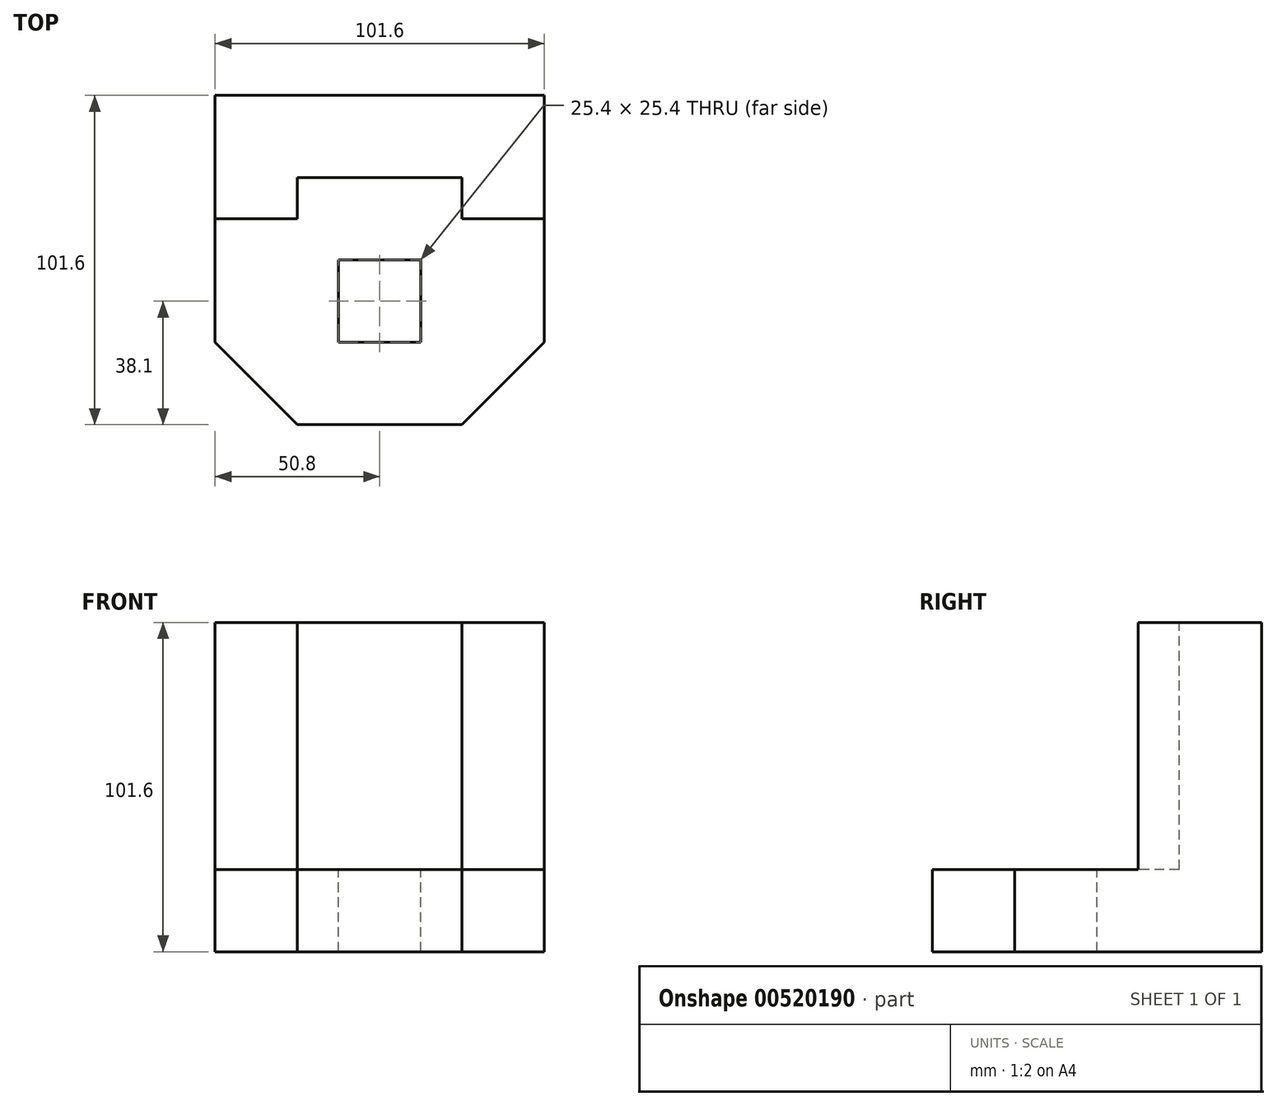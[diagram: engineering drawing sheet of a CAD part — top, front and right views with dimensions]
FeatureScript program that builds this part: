
annotation { "Feature Type Name" : "Feature", "Feature Type Description" : "" }
export const myFeature = defineFeature(function(context is Context, id is Id, definition is map)
    precondition{}
    {
        {
            var Q0;
            Q0=qCreatedBy(makeId("Right.planeOp"),FACE);
            var sketch = newSketch(context, id + "F0", { "sketchPlane" : qUnion([Q0])});
            skLineSegment(sketch, "E0.bottom", {"start": v(0, 0) * mm, "end": v(101.6, 0) * mm});
            skLineSegment(sketch, "E0.top", {"start": v(0, -101.6) * mm, "end": v(101.6, -101.6) * mm});
            skLineSegment(sketch, "E0.left", {"start": v(0, 0) * mm, "end": v(0, -101.6) * mm});
            skLineSegment(sketch, "E0.right", {"start": v(101.6, 0) * mm, "end": v(101.6, -101.6) * mm});
            skSolve(sketch);
        }
        {
            var Q0;
            Q0=makeQuery(id+"F0.imprint","IMPRINT",FACE,{"disambiguationData":[TD([[makeQuery(id+"F0.imprint","IMPRINT",EDGE,{"derivedFrom":sQuery(id+"F0.wireOp",EDGE,"E0.bottom")}),-1.0]])]});
            extrude(context, id + "F1", {"entities" : qUnion([Q0]), "oppositeDirection" : true, "depth" : 101.6 * mm, "offsetDistance" : 25.4 * mm});
        }
        {
            var Q0;
            Q0=makeQuery(id+"F1.opExtrude","SWEPT_FACE",FACE,{"disambiguationData":[OSD([sQuery(id+"F0.wireOp",EDGE,"E0.bottom")])]});
            var sketch = newSketch(context, id + "F2", { "sketchPlane" : qUnion([Q0])});
            skLineSegment(sketch, "E1", {"start": v(-101.6, 101.6) * mm, "end": v(-101.6, 63.5) * mm});
            skLineSegment(sketch, "E2", {"start": v(-101.6, 63.5) * mm, "end": v(-76.2, 63.5) * mm});
            skLineSegment(sketch, "E3", {"start": v(-76.2, 63.5) * mm, "end": v(-76.2, 82.55) * mm});
            skPoint(sketch, "E3.endSnap0", {"position": v(-101.6, 82.55) * mm});
            skLineSegment(sketch, "E4", {"start": v(-76.2, 82.55) * mm, "end": v(-25.4, 82.55) * mm});
            skLineSegment(sketch, "E5", {"start": v(-25.4, 82.55) * mm, "end": v(-25.4, 63.5) * mm});
            skLineSegment(sketch, "E6", {"start": v(-25.4, 63.5) * mm, "end": v(0, 63.5) * mm});
            skLineSegment(sketch, "E7", {"start": v(0, 63.5) * mm, "end": v(-76.2, 63.5) * mm});
            skLineSegment(sketch, "E8", {"start": v(-25.4, 63.5) * mm, "end": v(-76.2, 63.5) * mm});
            skSolve(sketch);
        }
        {
            var Q0;
            {var subQ3=sQuery(id+"F2.wireOp",EDGE,"E2");Q0=makeQuery(id+"F2.imprint","IMPRINT",FACE,{"disambiguationData":[TD([[makeQuery(id+"F2.imprint","IMPRINT",EDGE,{"derivedFrom":subQ3}),-1.0]])]});}
            extrude(context, id + "F3", {"entities" : qUnion([Q0]), "operationType" : NewBodyOperationType.REMOVE, "oppositeDirection" : true, "depth" : 76.2 * mm, "offsetDistance" : 25.4 * mm});
        }
        {
            var Q0;
            Q0=makeQuery(id+"F1.opExtrude","SWEPT_FACE",FACE,{"disambiguationData":[OSD([sQuery(id+"F0.wireOp",EDGE,"E0.bottom")])]});
            var sketch = newSketch(context, id + "F4", { "sketchPlane" : qUnion([Q0])});
            skLineSegment(sketch, "E9", {"start": v(-101.6, 101.6) * mm, "end": v(-101.6, 63.5) * mm});
            skLineSegment(sketch, "E10", {"start": v(-101.6, 63.5) * mm, "end": v(-76.2, 63.5) * mm});
            skLineSegment(sketch, "E11", {"start": v(-76.2, 63.5) * mm, "end": v(-76.2, 76.2) * mm});
            skLineSegment(sketch, "E12", {"start": v(-76.2, 76.2) * mm, "end": v(-25.4, 76.2) * mm});
            skLineSegment(sketch, "E13", {"start": v(-25.4, 76.2) * mm, "end": v(-25.4, 63.5) * mm});
            skLineSegment(sketch, "E14", {"start": v(-25.4, 63.5) * mm, "end": v(0, 63.5) * mm});
            skLineSegment(sketch, "E15", {"start": v(0, 63.5) * mm, "end": v(-25.4, 63.5) * mm});
            skLineSegment(sketch, "E16", {"start": v(-76.2, 63.5) * mm, "end": v(-25.4, 63.5) * mm});
            skSolve(sketch);
        }
        {
            var Q0;
            Q0=makeQuery(id+"F4.imprint","IMPRINT",FACE,{"disambiguationData":[TD([[makeQuery(id+"F4.imprint","IMPRINT",EDGE,{"derivedFrom":sQuery(id+"F4.wireOp",EDGE,"E11")}),-1.0]])]});
            extrude(context, id + "F5", {"entities" : qUnion([Q0]), "operationType" : NewBodyOperationType.REMOVE, "oppositeDirection" : true, "depth" : 76.2 * mm, "offsetDistance" : 25.4 * mm});
        }
        {
            var Q0;
            Q0=makeQuery(id+"F3.boolean.opBoolean","COPY",FACE,{"derivedFrom":makeQuery(id+"F3.opExtrude","CAP_FACE",FACE,{"disambiguationData":[OSD([sQuery(id+"F0.wireOp",EDGE,"E0.bottom"),sQuery(id+"F0.wireOp",EDGE,"E0.left"),sQuery(id+"F2.wireOp",EDGE,"E2"),sQuery(id+"F2.wireOp",EDGE,"E7"),sQuery(id+"F2.wireOp",EDGE,"E8")])],"isStart":false})});
            var sketch = newSketch(context, id + "F6", { "sketchPlane" : qUnion([Q0])});
            skLineSegment(sketch, "E17.bottom", {"start": v(-101.6, 0) * mm, "end": v(-76.2, 0) * mm});
            skLineSegment(sketch, "E17.top", {"start": v(-101.6, 25.4) * mm, "end": v(-76.2, 25.4) * mm});
            skLineSegment(sketch, "E17.left", {"start": v(-101.6, 0) * mm, "end": v(-101.6, 25.4) * mm});
            skLineSegment(sketch, "E17.right", {"start": v(-76.2, 0) * mm, "end": v(-76.2, 25.4) * mm});
            skLineSegment(sketch, "E18.bottom", {"start": v(0, 0) * mm, "end": v(-25.4, 0) * mm});
            skLineSegment(sketch, "E18.top", {"start": v(0, 25.4) * mm, "end": v(-25.4, 25.4) * mm});
            skLineSegment(sketch, "E18.left", {"start": v(0, 0) * mm, "end": v(0, 25.4) * mm});
            skLineSegment(sketch, "E18.right", {"start": v(-25.4, 0) * mm, "end": v(-25.4, 25.4) * mm});
            skLineSegment(sketch, "E19", {"start": v(-76.2, 76.2) * mm, "end": v(-76.2, 50.8) * mm});
            skLineSegment(sketch, "E20", {"start": v(-76.2, 50.8) * mm, "end": v(-76.2, 76.2) * mm});
            skLineSegment(sketch, "E21", {"start": v(-25.4, 76.2) * mm, "end": v(-76.2, 76.2) * mm});
            skLineSegment(sketch, "E22", {"start": v(-25.4, 76.2) * mm, "end": v(-25.4, 50.8) * mm});
            skLineSegment(sketch, "E23", {"start": v(-25.4, 50.8) * mm, "end": v(-76.2, 50.8) * mm});
            skLineSegment(sketch, "E24", {"start": v(-76.2, 25.4) * mm, "end": v(-76.2, 50.8) * mm});
            skLineSegment(sketch, "E25", {"start": v(-25.4, 50.8) * mm, "end": v(-25.4, 25.4) * mm});
            skLineSegment(sketch, "E26", {"start": v(-76.2, 25.4) * mm, "end": v(-25.4, 25.4) * mm});
            skLineSegment(sketch, "E27", {"start": v(-50.8, 50.8) * mm, "end": v(-50.8, 25.4) * mm});
            skLineSegment(sketch, "E28", {"start": v(-50.8, 25.4) * mm, "end": v(-76.2, 25.4) * mm});
            skLineSegment(sketch, "E29", {"start": v(-101.6, 25.4) * mm, "end": v(-76.2, 0) * mm});
            skLineSegment(sketch, "E30", {"start": v(-25.4, 0) * mm, "end": v(0, 25.4) * mm});
            skLineSegment(sketch, "E31", {"start": v(-50.8, 50.8) * mm, "end": v(-63.5, 50.8) * mm});
            skLineSegment(sketch, "E32", {"start": v(-63.5, 50.8) * mm, "end": v(-50.8, 50.8) * mm});
            skLineSegment(sketch, "E33", {"start": v(-50.8, 50.8) * mm, "end": v(-38.1, 50.8) * mm});
            skLineSegment(sketch, "E34", {"start": v(-38.1, 50.8) * mm, "end": v(-38.1, 25.4) * mm});
            skLineSegment(sketch, "E35", {"start": v(-38.1, 25.4) * mm, "end": v(-63.5, 25.4) * mm});
            skLineSegment(sketch, "E36", {"start": v(-63.5, 25.4) * mm, "end": v(-63.5, 50.8) * mm});
            skSolve(sketch);
        }
        {
            var Q0;
            Q0=makeQuery(id+"F6.imprint","IMPRINT",FACE,{"disambiguationData":[TD([[makeQuery(id+"F6.imprint","IMPRINT",EDGE,{"derivedFrom":sQuery(id+"F6.wireOp",EDGE,"E17.bottom")}),1.0]])]});
            var Q1;
            Q1=makeQuery(id+"F6.imprint","IMPRINT",FACE,{"disambiguationData":[TD([[makeQuery(id+"F6.imprint","IMPRINT",EDGE,{"derivedFrom":sQuery(id+"F6.wireOp",EDGE,"E18.bottom")}),1.0]])]});
            var Q2;
            {var subQ0=sQuery(id+"F6.wireOp",EDGE,"E27");Q2=makeQuery(id+"F6.imprint","IMPRINT",FACE,{"disambiguationData":[TD([[makeQuery(id+"F6.imprint","IMPRINT",EDGE,{"derivedFrom":subQ0}),-1.0]])]});}
            var Q3;
            {var subQ0=sQuery(id+"F6.wireOp",EDGE,"E27");Q3=makeQuery(id+"F6.imprint","IMPRINT",FACE,{"disambiguationData":[TD([[makeQuery(id+"F6.imprint","IMPRINT",EDGE,{"derivedFrom":subQ0}),1.0]])]});}
            extrude(context, id + "F7", {"entities" : qUnion([Q0, Q1, Q2, Q3]), "operationType" : NewBodyOperationType.REMOVE, "oppositeDirection" : true, "depth" : 68.33 * mm, "offsetDistance" : 25.4 * mm});
        }
    });
